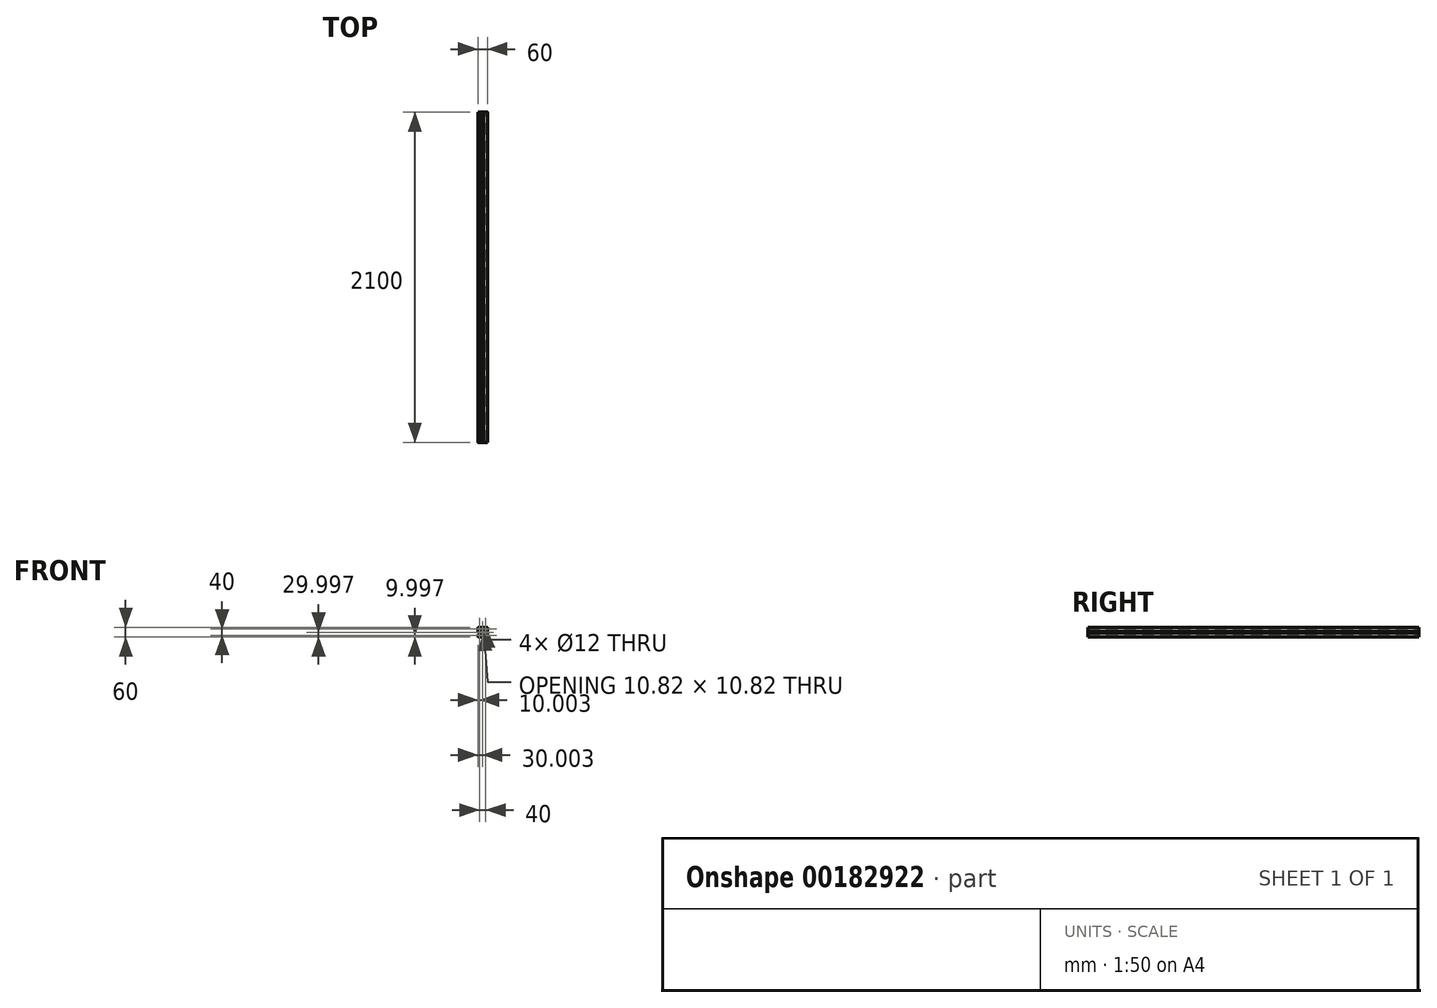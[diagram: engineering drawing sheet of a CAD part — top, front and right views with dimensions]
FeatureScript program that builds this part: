
annotation { "Feature Type Name" : "Feature", "Feature Type Description" : "" }
export const myFeature = defineFeature(function(context is Context, id is Id, definition is map)
    precondition{}
    {
        {
            var Q0;
            Q0=qCreatedBy(makeId("Front.planeOp"),FACE);
            var sketch = newSketch(context, id + "F0", { "sketchPlane" : qUnion([Q0])});
            skLineSegment(sketch, "E0", {"start": v(14.78, 10.14) * mm, "end": v(19.78, 10.14) * mm});
            skLineSegment(sketch, "E1", {"start": v(14.78, -29.86) * mm, "end": v(19.78, -29.86) * mm});
            skLineSegment(sketch, "E2", {"start": v(25.58, -9.86) * mm, "end": v(-39.63, -9.86) * mm});
            skLineSegment(sketch, "E3", {"start": v(12.78, 12.14) * mm, "end": v(12.78, 17.14) * mm});
            skLineSegment(sketch, "E4", {"start": v(-27.22, 12.14) * mm, "end": v(-27.22, 17.14) * mm});
            skLineSegment(sketch, "E5", {"start": v(-7.22, -43.01) * mm, "end": v(-7.22, 22.82) * mm});
            skLineSegment(sketch, "E6", {"start": v(11.78, 10.14) * mm, "end": v(13.78, 10.14) * mm});
            skLineSegment(sketch, "E7", {"start": v(12.78, 9.14) * mm, "end": v(12.78, 11.14) * mm});
            skLineSegment(sketch, "E8", {"start": v(10.78, 10.14) * mm, "end": v(5.78, 10.14) * mm});
            skLineSegment(sketch, "E9", {"start": v(12.78, 8.14) * mm, "end": v(12.78, 3.14) * mm});
            skLineSegment(sketch, "E10", {"start": v(-28.22, 10.14) * mm, "end": v(-26.22, 10.14) * mm});
            skLineSegment(sketch, "E11", {"start": v(-27.22, 9.14) * mm, "end": v(-27.22, 11.14) * mm});
            skLineSegment(sketch, "E12", {"start": v(-25.22, 10.14) * mm, "end": v(-20.22, 10.14) * mm});
            skLineSegment(sketch, "E13", {"start": v(-27.22, 8.14) * mm, "end": v(-27.22, 3.14) * mm});
            skLineSegment(sketch, "E14", {"start": v(-28.22, -29.86) * mm, "end": v(-26.22, -29.86) * mm});
            skLineSegment(sketch, "E15", {"start": v(-27.22, -30.86) * mm, "end": v(-27.22, -28.86) * mm});
            skLineSegment(sketch, "E16", {"start": v(-25.22, -29.86) * mm, "end": v(-20.22, -29.86) * mm});
            skLineSegment(sketch, "E17", {"start": v(-27.22, -31.86) * mm, "end": v(-27.22, -36.86) * mm});
            skLineSegment(sketch, "E18", {"start": v(-27.22, -27.86) * mm, "end": v(-27.22, -22.86) * mm});
            skLineSegment(sketch, "E19", {"start": v(11.78, -29.86) * mm, "end": v(13.78, -29.86) * mm});
            skLineSegment(sketch, "E20", {"start": v(12.78, -30.86) * mm, "end": v(12.78, -28.86) * mm});
            skLineSegment(sketch, "E21", {"start": v(10.78, -29.86) * mm, "end": v(5.78, -29.86) * mm});
            skLineSegment(sketch, "E22", {"start": v(12.78, -31.86) * mm, "end": v(12.78, -36.86) * mm});
            skLineSegment(sketch, "E23", {"start": v(12.78, -27.86) * mm, "end": v(12.78, -22.86) * mm});
            skLineSegment(sketch, "E24", {"start": v(-1.71, -15.37) * mm, "end": v(-13.23, -3.85) * mm});
            skLineSegment(sketch, "E25", {"start": v(-12.72, -15.37) * mm, "end": v(-1.2, -3.85) * mm});
            skArc(sketch, "E26", {"start": v(-7.2, -39.26) * mm, "mid": v(-7.22, -39.26) * mm, "end": v(-7.23, -39.26) * mm});
            skLineSegment(sketch, "E27", {"start": v(-29.22, 10.14) * mm, "end": v(-34.22, 10.14) * mm});
            skLineSegment(sketch, "E28", {"start": v(-29.22, -29.86) * mm, "end": v(-34.22, -29.86) * mm});
            skCircle(sketch, "E29", {"center": v(-27.22, -29.86) * mm, "radius": 6 * mm});
            skCircle(sketch, "E30", {"center": v(12.78, 10.14) * mm, "radius": 6 * mm});
            skCircle(sketch, "E31", {"center": v(-27.22, 10.14) * mm, "radius": 6 * mm});
            skCircle(sketch, "E32", {"center": v(12.78, -29.86) * mm, "radius": 6 * mm});
            skLineSegment(sketch, "E33", {"start": v(-44.48, -25.98) * mm, "end": v(-13.37, -12.52) * mm});
            skLineSegment(sketch, "E34", {"start": v(-1.07, -7.2) * mm, "end": v(0.5, -6.53) * mm});
            skLineSegment(sketch, "E35", {"start": v(-2.63, -7.88) * mm, "end": v(-11.8, -11.85) * mm});
            skLineSegment(sketch, "E36", {"start": v(-0.89, -7.62) * mm, "end": v(-2.63, -7.88) * mm});
            skLineSegment(sketch, "E37", {"start": v(-2.63, -7.88) * mm, "end": v(-1.25, -6.79) * mm});
            skLineSegment(sketch, "E38", {"start": v(-2.63, -7.88) * mm, "end": v(-1.07, -7.2) * mm});
            skLineSegment(sketch, "E39", {"start": v(-13.55, -12.1) * mm, "end": v(-11.8, -11.85) * mm});
            skLineSegment(sketch, "E40", {"start": v(-11.8, -11.85) * mm, "end": v(-13.19, -12.94) * mm});
            skLineSegment(sketch, "E41", {"start": v(-11.8, -11.85) * mm, "end": v(-13.37, -12.52) * mm});
            skLineSegment(sketch, "E42", {"start": v(20.63, 10.14) * mm, "end": v(38.1, 10.14) * mm});
            skLineSegment(sketch, "E43", {"start": v(20.63, -29.86) * mm, "end": v(38.1, -29.86) * mm});
            skLineSegment(sketch, "E44", {"start": v(36.99, 8.44) * mm, "end": v(36.99, -28.16) * mm});
            skLineSegment(sketch, "E45", {"start": v(36.53, 8.44) * mm, "end": v(36.99, 10.14) * mm});
            skLineSegment(sketch, "E46", {"start": v(36.99, 10.14) * mm, "end": v(37.44, 8.44) * mm});
            skLineSegment(sketch, "E47", {"start": v(36.99, 10.14) * mm, "end": v(36.99, 8.44) * mm});
            skLineSegment(sketch, "E48", {"start": v(37.44, -28.16) * mm, "end": v(36.99, -29.86) * mm});
            skLineSegment(sketch, "E49", {"start": v(36.99, -29.86) * mm, "end": v(36.53, -28.16) * mm});
            skLineSegment(sketch, "E50", {"start": v(36.99, -29.86) * mm, "end": v(36.99, -28.16) * mm});
            skLineSegment(sketch, "E51", {"start": v(22.18, -16.16) * mm, "end": v(18.38, -16.16) * mm});
            skArc(sketch, "E52", {"start": v(18.38, -16.16) * mm, "mid": v(17.96, -16.34) * mm, "end": v(17.78, -16.76) * mm});
            skLineSegment(sketch, "E53", {"start": v(17.78, -16.76) * mm, "end": v(17.78, -19.56) * mm});
            skArc(sketch, "E54", {"start": v(17.78, -19.56) * mm, "mid": v(17.6, -19.99) * mm, "end": v(17.18, -20.16) * mm});
            skLineSegment(sketch, "E55", {"start": v(17.18, -20.16) * mm, "end": v(6.14, -20.16) * mm});
            skArc(sketch, "E56", {"start": v(6.14, -20.16) * mm, "mid": v(5.9, -20.11) * mm, "end": v(5.7, -19.97) * mm});
            skArc(sketch, "E57", {"start": v(5.7, -19.97) * mm, "mid": v(2.89, -15.52) * mm, "end": v(1.8, -10.37) * mm});
            skLineSegment(sketch, "E58", {"start": v(1.8, -10.37) * mm, "end": v(1.28, -9.86) * mm});
            skLineSegment(sketch, "E59", {"start": v(1.28, -9.86) * mm, "end": v(1.8, -9.35) * mm});
            skArc(sketch, "E60", {"start": v(1.8, -9.35) * mm, "mid": v(2.89, -4.2) * mm, "end": v(5.7, 0.24) * mm});
            skArc(sketch, "E61", {"start": v(5.7, 0.24) * mm, "mid": v(5.9, 0.39) * mm, "end": v(6.14, 0.44) * mm});
            skLineSegment(sketch, "E62", {"start": v(6.14, 0.44) * mm, "end": v(17.18, 0.44) * mm});
            skArc(sketch, "E63", {"start": v(17.18, 0.44) * mm, "mid": v(17.6, 0.26) * mm, "end": v(17.78, -0.16) * mm});
            skLineSegment(sketch, "E64", {"start": v(17.78, -0.16) * mm, "end": v(17.78, -2.96) * mm});
            skArc(sketch, "E65", {"start": v(17.78, -2.96) * mm, "mid": v(17.96, -3.39) * mm, "end": v(18.38, -3.56) * mm});
            skLineSegment(sketch, "E66", {"start": v(18.38, -3.56) * mm, "end": v(22.18, -3.56) * mm});
            skArc(sketch, "E67", {"start": v(22.18, -3.56) * mm, "mid": v(22.6, -3.39) * mm, "end": v(22.78, -2.96) * mm});
            skLineSegment(sketch, "E68", {"start": v(22.78, -2.96) * mm, "end": v(22.78, 18.14) * mm});
            skArc(sketch, "E69", {"start": v(22.78, 18.14) * mm, "mid": v(22.2, 19.55) * mm, "end": v(20.78, 20.14) * mm});
            skLineSegment(sketch, "E70", {"start": v(20.78, 20.14) * mm, "end": v(-0.32, 20.14) * mm});
            skArc(sketch, "E71", {"start": v(-0.32, 20.14) * mm, "mid": v(-0.74, 19.96) * mm, "end": v(-0.92, 19.54) * mm});
            skLineSegment(sketch, "E72", {"start": v(-0.92, 19.54) * mm, "end": v(-0.92, 15.74) * mm});
            skArc(sketch, "E73", {"start": v(-0.92, 15.74) * mm, "mid": v(-0.74, 15.31) * mm, "end": v(-0.32, 15.14) * mm});
            skLineSegment(sketch, "E74", {"start": v(-0.32, 15.14) * mm, "end": v(2.48, 15.14) * mm});
            skArc(sketch, "E75", {"start": v(2.48, 15.14) * mm, "mid": v(2.9, 14.96) * mm, "end": v(3.08, 14.54) * mm});
            skLineSegment(sketch, "E76", {"start": v(3.08, 14.54) * mm, "end": v(3.08, 3.5) * mm});
            skArc(sketch, "E77", {"start": v(3.08, 3.5) * mm, "mid": v(3.03, 3.25) * mm, "end": v(2.89, 3.05) * mm});
            skArc(sketch, "E78", {"start": v(2.89, 3.05) * mm, "mid": v(-1.56, 0.24) * mm, "end": v(-6.7, -0.85) * mm});
            skLineSegment(sketch, "E79", {"start": v(-6.7, -0.85) * mm, "end": v(-7.22, -1.36) * mm});
            skLineSegment(sketch, "E80", {"start": v(-7.22, -1.36) * mm, "end": v(-7.73, -0.85) * mm});
            skArc(sketch, "E81", {"start": v(-7.73, -0.85) * mm, "mid": v(-12.87, 0.24) * mm, "end": v(-17.32, 3.05) * mm});
            skArc(sketch, "E82", {"start": v(-17.32, 3.05) * mm, "mid": v(-17.47, 3.25) * mm, "end": v(-17.52, 3.5) * mm});
            skLineSegment(sketch, "E83", {"start": v(-17.52, 3.5) * mm, "end": v(-17.52, 14.54) * mm});
            skArc(sketch, "E84", {"start": v(-17.52, 14.54) * mm, "mid": v(-17.34, 14.96) * mm, "end": v(-16.92, 15.14) * mm});
            skLineSegment(sketch, "E85", {"start": v(-16.92, 15.14) * mm, "end": v(-14.12, 15.14) * mm});
            skArc(sketch, "E86", {"start": v(-14.12, 15.14) * mm, "mid": v(-13.7, 15.31) * mm, "end": v(-13.52, 15.74) * mm});
            skLineSegment(sketch, "E87", {"start": v(-13.52, 15.74) * mm, "end": v(-13.52, 19.54) * mm});
            skArc(sketch, "E88", {"start": v(-13.52, 19.54) * mm, "mid": v(-13.7, 19.96) * mm, "end": v(-14.12, 20.14) * mm});
            skLineSegment(sketch, "E89", {"start": v(-14.12, 20.14) * mm, "end": v(-35.22, 20.14) * mm});
            skArc(sketch, "E90", {"start": v(-35.22, 20.14) * mm, "mid": v(-36.63, 19.55) * mm, "end": v(-37.22, 18.14) * mm});
            skLineSegment(sketch, "E91", {"start": v(-37.22, 18.14) * mm, "end": v(-37.22, -2.96) * mm});
            skArc(sketch, "E92", {"start": v(-37.22, -2.96) * mm, "mid": v(-37.04, -3.39) * mm, "end": v(-36.62, -3.56) * mm});
            skLineSegment(sketch, "E93", {"start": v(-36.62, -3.56) * mm, "end": v(-32.82, -3.56) * mm});
            skArc(sketch, "E94", {"start": v(-32.82, -3.56) * mm, "mid": v(-32.4, -3.39) * mm, "end": v(-32.22, -2.96) * mm});
            skLineSegment(sketch, "E95", {"start": v(-32.22, -2.96) * mm, "end": v(-32.22, -0.16) * mm});
            skArc(sketch, "E96", {"start": v(-32.22, -0.16) * mm, "mid": v(-32.04, 0.26) * mm, "end": v(-31.62, 0.44) * mm});
            skLineSegment(sketch, "E97", {"start": v(-31.62, 0.44) * mm, "end": v(-20.57, 0.44) * mm});
            skArc(sketch, "E98", {"start": v(-20.57, 0.44) * mm, "mid": v(-20.33, 0.39) * mm, "end": v(-20.13, 0.24) * mm});
            skArc(sketch, "E99", {"start": v(-20.13, 0.24) * mm, "mid": v(-17.32, -4.2) * mm, "end": v(-16.23, -9.35) * mm});
            skLineSegment(sketch, "E100", {"start": v(-16.23, -9.35) * mm, "end": v(-15.72, -9.86) * mm});
            skLineSegment(sketch, "E101", {"start": v(-15.72, -9.86) * mm, "end": v(-16.23, -10.37) * mm});
            skArc(sketch, "E102", {"start": v(-16.23, -10.37) * mm, "mid": v(-17.32, -15.52) * mm, "end": v(-20.13, -19.97) * mm});
            skArc(sketch, "E103", {"start": v(-20.13, -19.97) * mm, "mid": v(-20.33, -20.11) * mm, "end": v(-20.57, -20.16) * mm});
            skLineSegment(sketch, "E104", {"start": v(-20.57, -20.16) * mm, "end": v(-31.62, -20.16) * mm});
            skArc(sketch, "E105", {"start": v(-31.62, -20.16) * mm, "mid": v(-32.04, -19.99) * mm, "end": v(-32.22, -19.56) * mm});
            skLineSegment(sketch, "E106", {"start": v(-32.22, -19.56) * mm, "end": v(-32.22, -16.76) * mm});
            skArc(sketch, "E107", {"start": v(-32.22, -16.76) * mm, "mid": v(-32.4, -16.34) * mm, "end": v(-32.82, -16.16) * mm});
            skLineSegment(sketch, "E108", {"start": v(-32.82, -16.16) * mm, "end": v(-36.62, -16.16) * mm});
            skArc(sketch, "E109", {"start": v(-36.62, -16.16) * mm, "mid": v(-37.04, -16.34) * mm, "end": v(-37.22, -16.76) * mm});
            skLineSegment(sketch, "E110", {"start": v(-37.22, -16.76) * mm, "end": v(-37.22, -37.86) * mm});
            skArc(sketch, "E111", {"start": v(-37.22, -37.86) * mm, "mid": v(-36.63, -39.28) * mm, "end": v(-35.22, -39.86) * mm});
            skLineSegment(sketch, "E112", {"start": v(-35.22, -39.86) * mm, "end": v(-14.12, -39.86) * mm});
            skArc(sketch, "E113", {"start": v(-14.12, -39.86) * mm, "mid": v(-13.7, -39.69) * mm, "end": v(-13.52, -39.26) * mm});
            skLineSegment(sketch, "E114", {"start": v(-13.52, -39.26) * mm, "end": v(-13.52, -35.46) * mm});
            skArc(sketch, "E115", {"start": v(-13.52, -35.46) * mm, "mid": v(-13.7, -35.04) * mm, "end": v(-14.12, -34.86) * mm});
            skLineSegment(sketch, "E116", {"start": v(-14.12, -34.86) * mm, "end": v(-16.92, -34.86) * mm});
            skArc(sketch, "E117", {"start": v(-16.92, -34.86) * mm, "mid": v(-17.34, -34.69) * mm, "end": v(-17.52, -34.26) * mm});
            skLineSegment(sketch, "E118", {"start": v(-17.52, -34.26) * mm, "end": v(-17.52, -23.22) * mm});
            skArc(sketch, "E119", {"start": v(-17.52, -23.22) * mm, "mid": v(-17.47, -22.98) * mm, "end": v(-17.32, -22.78) * mm});
            skArc(sketch, "E120", {"start": v(-17.32, -22.78) * mm, "mid": v(-12.87, -19.97) * mm, "end": v(-7.73, -18.87) * mm});
            skLineSegment(sketch, "E121", {"start": v(-7.73, -18.87) * mm, "end": v(-7.22, -18.36) * mm});
            skLineSegment(sketch, "E122", {"start": v(-7.22, -18.36) * mm, "end": v(-6.7, -18.87) * mm});
            skArc(sketch, "E123", {"start": v(-6.7, -18.87) * mm, "mid": v(-1.56, -19.97) * mm, "end": v(2.89, -22.78) * mm});
            skArc(sketch, "E124", {"start": v(2.89, -22.78) * mm, "mid": v(3.03, -22.98) * mm, "end": v(3.08, -23.22) * mm});
            skLineSegment(sketch, "E125", {"start": v(3.08, -23.22) * mm, "end": v(3.08, -34.26) * mm});
            skArc(sketch, "E126", {"start": v(3.08, -34.26) * mm, "mid": v(2.9, -34.69) * mm, "end": v(2.48, -34.86) * mm});
            skLineSegment(sketch, "E127", {"start": v(2.48, -34.86) * mm, "end": v(-0.32, -34.86) * mm});
            skArc(sketch, "E128", {"start": v(-0.32, -34.86) * mm, "mid": v(-0.74, -35.04) * mm, "end": v(-0.92, -35.46) * mm});
            skLineSegment(sketch, "E129", {"start": v(-0.92, -35.46) * mm, "end": v(-0.92, -39.26) * mm});
            skArc(sketch, "E130", {"start": v(-0.92, -39.26) * mm, "mid": v(-0.74, -39.69) * mm, "end": v(-0.32, -39.86) * mm});
            skLineSegment(sketch, "E131", {"start": v(-0.32, -39.86) * mm, "end": v(20.78, -39.86) * mm});
            skArc(sketch, "E132", {"start": v(20.78, -39.86) * mm, "mid": v(22.2, -39.28) * mm, "end": v(22.78, -37.86) * mm});
            skLineSegment(sketch, "E133", {"start": v(22.78, -37.86) * mm, "end": v(22.78, -16.76) * mm});
            skArc(sketch, "E134", {"start": v(22.78, -16.76) * mm, "mid": v(22.6, -16.34) * mm, "end": v(22.18, -16.16) * mm});
            skArc(sketch, "E135", {"start": v(-9.6, -14.26) * mm, "mid": v(-7.22, -14.86) * mm, "end": v(-4.84, -14.26) * mm});
            skArc(sketch, "E136", {"start": v(-4.84, -14.26) * mm, "mid": v(-4.47, -14.2) * mm, "end": v(-4.13, -14.36) * mm});
            skLineSegment(sketch, "E137", {"start": v(-4.13, -14.36) * mm, "end": v(-3.4, -15.1) * mm});
            skArc(sketch, "E138", {"start": v(-3.4, -15.1) * mm, "mid": v(-2.97, -15.27) * mm, "end": v(-2.55, -15.1) * mm});
            skLineSegment(sketch, "E139", {"start": v(-2.55, -15.1) * mm, "end": v(-1.98, -14.53) * mm});
            skArc(sketch, "E140", {"start": v(-1.98, -14.53) * mm, "mid": v(-1.8, -14.1) * mm, "end": v(-1.98, -13.68) * mm});
            skLineSegment(sketch, "E141", {"start": v(-1.98, -13.68) * mm, "end": v(-2.71, -12.95) * mm});
            skArc(sketch, "E142", {"start": v(-2.71, -12.95) * mm, "mid": v(-2.88, -12.61) * mm, "end": v(-2.82, -12.24) * mm});
            skArc(sketch, "E143", {"start": v(-2.82, -12.24) * mm, "mid": v(-2.22, -9.86) * mm, "end": v(-2.82, -7.48) * mm});
            skArc(sketch, "E144", {"start": v(-2.82, -7.48) * mm, "mid": v(-2.88, -7.11) * mm, "end": v(-2.71, -6.78) * mm});
            skLineSegment(sketch, "E145", {"start": v(-2.71, -6.78) * mm, "end": v(-1.98, -6.04) * mm});
            skArc(sketch, "E146", {"start": v(-1.98, -6.04) * mm, "mid": v(-1.8, -5.62) * mm, "end": v(-1.98, -5.2) * mm});
            skLineSegment(sketch, "E147", {"start": v(-1.98, -5.2) * mm, "end": v(-2.55, -4.63) * mm});
            skArc(sketch, "E148", {"start": v(-2.55, -4.63) * mm, "mid": v(-2.97, -4.45) * mm, "end": v(-3.4, -4.63) * mm});
            skLineSegment(sketch, "E149", {"start": v(-3.4, -4.63) * mm, "end": v(-4.13, -5.36) * mm});
            skArc(sketch, "E150", {"start": v(-4.13, -5.36) * mm, "mid": v(-4.47, -5.53) * mm, "end": v(-4.84, -5.46) * mm});
            skArc(sketch, "E151", {"start": v(-4.84, -5.46) * mm, "mid": v(-7.22, -4.86) * mm, "end": v(-9.6, -5.46) * mm});
            skArc(sketch, "E152", {"start": v(-9.6, -5.46) * mm, "mid": v(-9.97, -5.53) * mm, "end": v(-10.3, -5.36) * mm});
            skLineSegment(sketch, "E153", {"start": v(-10.3, -5.36) * mm, "end": v(-11.04, -4.63) * mm});
            skArc(sketch, "E154", {"start": v(-11.04, -4.63) * mm, "mid": v(-11.46, -4.45) * mm, "end": v(-11.88, -4.63) * mm});
            skLineSegment(sketch, "E155", {"start": v(-11.88, -4.63) * mm, "end": v(-12.45, -5.2) * mm});
            skArc(sketch, "E156", {"start": v(-12.45, -5.2) * mm, "mid": v(-12.63, -5.62) * mm, "end": v(-12.45, -6.04) * mm});
            skLineSegment(sketch, "E157", {"start": v(-12.45, -6.04) * mm, "end": v(-11.72, -6.78) * mm});
            skArc(sketch, "E158", {"start": v(-11.72, -6.78) * mm, "mid": v(-11.55, -7.11) * mm, "end": v(-11.61, -7.48) * mm});
            skArc(sketch, "E159", {"start": v(-11.61, -7.48) * mm, "mid": v(-12.22, -9.86) * mm, "end": v(-11.61, -12.24) * mm});
            skArc(sketch, "E160", {"start": v(-11.61, -12.24) * mm, "mid": v(-11.55, -12.61) * mm, "end": v(-11.72, -12.95) * mm});
            skLineSegment(sketch, "E161", {"start": v(-11.72, -12.95) * mm, "end": v(-12.45, -13.68) * mm});
            skArc(sketch, "E162", {"start": v(-12.45, -13.68) * mm, "mid": v(-12.63, -14.1) * mm, "end": v(-12.45, -14.53) * mm});
            skLineSegment(sketch, "E163", {"start": v(-12.45, -14.53) * mm, "end": v(-11.88, -15.1) * mm});
            skArc(sketch, "E164", {"start": v(-11.88, -15.1) * mm, "mid": v(-11.46, -15.27) * mm, "end": v(-11.04, -15.1) * mm});
            skLineSegment(sketch, "E165", {"start": v(-11.04, -15.1) * mm, "end": v(-10.3, -14.36) * mm});
            skArc(sketch, "E166", {"start": v(-10.3, -14.36) * mm, "mid": v(-9.97, -14.2) * mm, "end": v(-9.6, -14.26) * mm});
            skSolve(sketch);
        }
        {
            var Q0;
            {var subQ4=sQuery(id+"F0.wireOp",EDGE,"E80");Q0=makeQuery(id+"F0.imprint","IMPRINT",FACE,{"disambiguationData":[TD([[makeQuery(id+"F0.imprint","IMPRINT",EDGE,{"derivedFrom":subQ4}),1.0]])]});}
            var Q1;
            {var subQ15=sQuery(id+"F0.wireOp",EDGE,"E59");Q1=makeQuery(id+"F0.imprint","IMPRINT",FACE,{"disambiguationData":[TD([[makeQuery(id+"F0.imprint","IMPRINT",EDGE,{"derivedFrom":subQ15}),1.0]])]});}
            var Q2;
            Q2=makeQuery(id+"F0.imprint","IMPRINT",FACE,{"disambiguationData":[TD([[makeQuery(id+"F0.imprint","IMPRINT",EDGE,{"derivedFrom":sQuery(id+"F0.wireOp",EDGE,"E51")}),1.0]])]});
            var Q3;
            {var subQ22=sQuery(id+"F0.wireOp",EDGE,"E41");Q3=makeQuery(id+"F0.imprint","IMPRINT",FACE,{"disambiguationData":[TD([[makeQuery(id+"F0.imprint","IMPRINT",EDGE,{"derivedFrom":subQ22}),1.0]])]});}
            var Q4;
            {var subQ1=sQuery(id+"F0.wireOp",EDGE,"E41");Q4=makeQuery(id+"F0.imprint","IMPRINT",FACE,{"disambiguationData":[TD([[makeQuery(id+"F0.imprint","IMPRINT",EDGE,{"derivedFrom":subQ1}),-1.0]])]});}
            var Q5;
            {var subQ0=sQuery(id+"F0.wireOp",EDGE,"E105");Q5=makeQuery(id+"F0.imprint","IMPRINT",FACE,{"disambiguationData":[TD([[makeQuery(id+"F0.imprint","IMPRINT",EDGE,{"derivedFrom":subQ0}),1.0]])]});}
            extrude(context, id + "F1", {"entities" : qUnion([Q0, Q1, Q2, Q3, Q4, Q5]), "endBound" : BoundingType.SYMMETRIC, "depth" : 2100 * mm});
        }
    });
